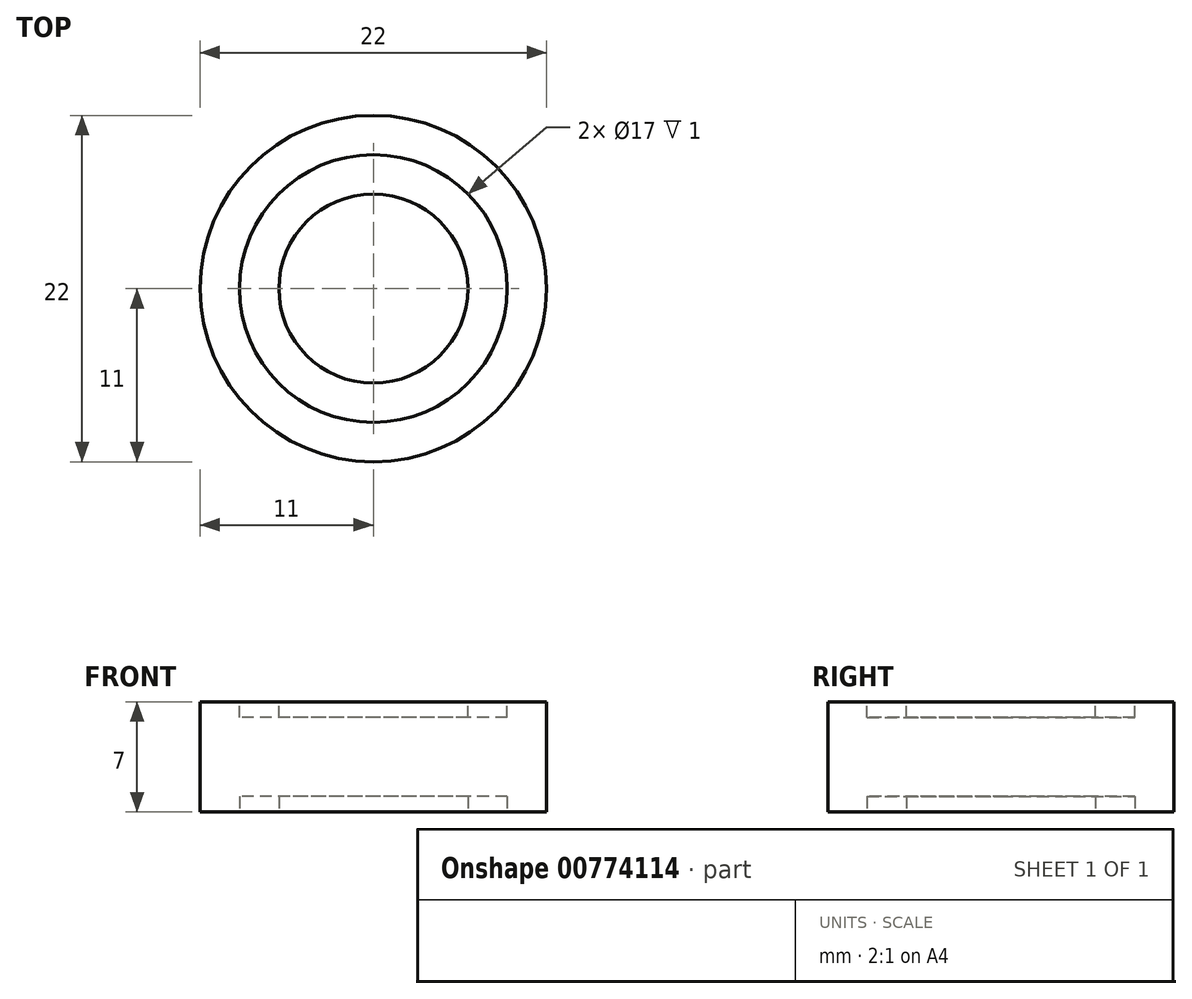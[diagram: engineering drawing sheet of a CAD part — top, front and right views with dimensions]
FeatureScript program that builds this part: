
annotation { "Feature Type Name" : "Feature", "Feature Type Description" : "" }
export const myFeature = defineFeature(function(context is Context, id is Id, definition is map)
    precondition{}
    {
        {
            var Q0;
            Q0=qCreatedBy(makeId("Top.planeOp"),FACE);
            var sketch = newSketch(context, id + "F0", { "sketchPlane" : qUnion([Q0])});
            skCircle(sketch, "E0", {"center": v(0, 0) * mm, "radius": 11 * mm});
            skSolve(sketch);
        }
        {
            var Q0;
            Q0=makeQuery(id+"F0.imprint","IMPRINT",FACE,{"disambiguationData":[TD([[makeQuery(id+"F0.imprint","IMPRINT",EDGE,{"derivedFrom":sQuery(id+"F0.wireOp",EDGE,"E0")}),1.0]])]});
            extrude(context, id + "F1", {"entities" : qUnion([Q0]), "depth" : 3.5 * mm, "offsetDistance" : 25 * mm, "hasSecondDirection" : true, "secondDirectionOppositeDirection" : true, "secondDirectionDepth" : 3.5 * mm});
        }
        {
            var Q0;
            Q0=qCreatedBy(makeId("Top.planeOp"),FACE);
            var sketch = newSketch(context, id + "F2", { "sketchPlane" : qUnion([Q0])});
            skCircle(sketch, "E1.cCircle", {"center": v(0, 22.13) * mm, "radius": 7.5 * mm, "construction": true});
            skLineSegment(sketch, "E1.0", {"start": v(4.33, 14.63) * mm, "end": v(-4.33, 14.63) * mm});
            skLineSegment(sketch, "E1.1", {"start": v(-4.33, 14.63) * mm, "end": v(-8.66, 22.13) * mm});
            skLineSegment(sketch, "E1.2", {"start": v(-8.66, 22.13) * mm, "end": v(-4.33, 29.63) * mm});
            skLineSegment(sketch, "E1.3", {"start": v(-4.33, 29.63) * mm, "end": v(4.33, 29.63) * mm});
            skLineSegment(sketch, "E1.4", {"start": v(4.33, 29.63) * mm, "end": v(8.66, 22.13) * mm});
            skLineSegment(sketch, "E1.5", {"start": v(8.66, 22.13) * mm, "end": v(4.33, 14.63) * mm});
            skPoint(sketch, "E1.0.midPoint", {"position": v(0, 14.63) * mm});
            skCircle(sketch, "E2.cCircle", {"center": v(0, 22.13) * mm, "radius": 5 * mm, "construction": true});
            skLineSegment(sketch, "E2.0", {"start": v(2.89, 17.13) * mm, "end": v(-2.89, 17.13) * mm});
            skLineSegment(sketch, "E2.1", {"start": v(-2.89, 17.13) * mm, "end": v(-5.77, 22.13) * mm});
            skLineSegment(sketch, "E2.2", {"start": v(-5.77, 22.13) * mm, "end": v(-2.89, 27.13) * mm});
            skLineSegment(sketch, "E2.3", {"start": v(-2.89, 27.13) * mm, "end": v(2.89, 27.13) * mm});
            skLineSegment(sketch, "E2.4", {"start": v(2.89, 27.13) * mm, "end": v(5.77, 22.13) * mm});
            skLineSegment(sketch, "E2.5", {"start": v(5.77, 22.13) * mm, "end": v(2.89, 17.13) * mm});
            skPoint(sketch, "E2.0.midPoint", {"position": v(0, 17.13) * mm});
            skCircle(sketch, "E3", {"center": v(0, 22.13) * mm, "radius": 5 * mm});
            skSolve(sketch);
        }
        {
            var Q0;
            Q0=makeQuery(id+"F2.imprint","IMPRINT",FACE,{"disambiguationData":[TD([[makeQuery(id+"F2.imprint","IMPRINT",EDGE,{"derivedFrom":sQuery(id+"F2.wireOp",EDGE,"E1.0")}),-1.0]])]});
            var Q1;
            {var subQ0=sQuery(id+"F2.wireOp",EDGE,"E2.1");var subQ1=sQuery(id+"F2.wireOp",EDGE,"E2.0");var subQ2=makeQuery(id+"F2.imprint","INTERSECT",VERTEX,{"derivedFrom":[subQ1,subQ0]});Q1=makeQuery(id+"F2.imprint","IMPRINT",FACE,{"disambiguationData":[TD([[makeQuery(id+"F2.imprint","IMPRINT",EDGE,{"disambiguationData":[TD([[subQ2,1.0]])],"derivedFrom":subQ1}),-1.0]])]});}
            var Q2;
            {var subQ0=sQuery(id+"F2.wireOp",EDGE,"E2.2");var subQ1=sQuery(id+"F2.wireOp",EDGE,"E2.1");var subQ2=makeQuery(id+"F2.imprint","INTERSECT",VERTEX,{"derivedFrom":[subQ1,subQ0]});Q2=makeQuery(id+"F2.imprint","IMPRINT",FACE,{"disambiguationData":[TD([[makeQuery(id+"F2.imprint","IMPRINT",EDGE,{"disambiguationData":[TD([[subQ2,1.0]])],"derivedFrom":subQ1}),-1.0]])]});}
            var Q3;
            {var subQ0=sQuery(id+"F2.wireOp",EDGE,"E2.3");var subQ1=sQuery(id+"F2.wireOp",EDGE,"E2.2");var subQ2=makeQuery(id+"F2.imprint","INTERSECT",VERTEX,{"derivedFrom":[subQ1,subQ0]});Q3=makeQuery(id+"F2.imprint","IMPRINT",FACE,{"disambiguationData":[TD([[makeQuery(id+"F2.imprint","IMPRINT",EDGE,{"disambiguationData":[TD([[subQ2,1.0]])],"derivedFrom":subQ1}),-1.0]])]});}
            var Q4;
            {var subQ0=sQuery(id+"F2.wireOp",EDGE,"E2.4");var subQ1=sQuery(id+"F2.wireOp",EDGE,"E2.3");var subQ2=makeQuery(id+"F2.imprint","INTERSECT",VERTEX,{"derivedFrom":[subQ1,subQ0]});Q4=makeQuery(id+"F2.imprint","IMPRINT",FACE,{"disambiguationData":[TD([[makeQuery(id+"F2.imprint","IMPRINT",EDGE,{"disambiguationData":[TD([[subQ2,1.0]])],"derivedFrom":subQ1}),-1.0]])]});}
            var Q5;
            {var subQ0=sQuery(id+"F2.wireOp",EDGE,"E2.5");var subQ1=sQuery(id+"F2.wireOp",EDGE,"E2.4");var subQ2=makeQuery(id+"F2.imprint","INTERSECT",VERTEX,{"derivedFrom":[subQ1,subQ0]});Q5=makeQuery(id+"F2.imprint","IMPRINT",FACE,{"disambiguationData":[TD([[makeQuery(id+"F2.imprint","IMPRINT",EDGE,{"disambiguationData":[TD([[subQ2,1.0]])],"derivedFrom":subQ1}),-1.0]])]});}
            var Q6;
            {var subQ0=sQuery(id+"F2.wireOp",EDGE,"E2.5");var subQ1=sQuery(id+"F2.wireOp",EDGE,"E2.0");var subQ2=makeQuery(id+"F2.imprint","INTERSECT",VERTEX,{"derivedFrom":[subQ1,subQ0]});Q6=makeQuery(id+"F2.imprint","IMPRINT",FACE,{"disambiguationData":[TD([[makeQuery(id+"F2.imprint","IMPRINT",EDGE,{"disambiguationData":[TD([[subQ2,-1.0]])],"derivedFrom":subQ1}),-1.0]])]});}
            extrude(context, id + "F3", {"entities" : qUnion([Q0, Q1, Q2, Q3, Q4, Q5, Q6]), "depth" : 3.5 * mm, "offsetDistance" : 25 * mm, "hasSecondDirection" : true, "secondDirectionOppositeDirection" : true, "secondDirectionDepth" : 3.5 * mm});
        }
        {
            var Q0;
            Q0=makeQuery(id+"F1.opExtrude","CAP_FACE",FACE,{"disambiguationData":[OSD([sQuery(id+"F0.wireOp",EDGE,"E0")])],"isStart":false});
            var sketch = newSketch(context, id + "F4", { "sketchPlane" : qUnion([Q0])});
            skPoint(sketch, "E4", {"position": v(0, 11) * mm});
            skCircle(sketch, "E5", {"center": v(0, 0) * mm, "radius": 11 * mm});
            skCircle(sketch, "E6", {"center": v(0, 0) * mm, "radius": 8.5 * mm});
            skCircle(sketch, "E7", {"center": v(0, 0) * mm, "radius": 6 * mm});
            skSolve(sketch);
        }
        {
            var Q0;
            Q0=makeQuery(id+"F4.imprint","IMPRINT",FACE,{"disambiguationData":[TD([[makeQuery(id+"F4.imprint","IMPRINT",EDGE,{"derivedFrom":sQuery(id+"F4.wireOp",EDGE,"E6")}),1.0]])]});
            extrude(context, id + "F5", {"entities" : qUnion([Q0]), "operationType" : NewBodyOperationType.REMOVE, "oppositeDirection" : true, "depth" : 1 * mm, "offsetDistance" : 25 * mm});
        }
        {
            var Q0;
            Q0=makeQuery(id+"F1.opExtrude","SWEPT_BODY",BODY,{"disambiguationData":[OSD([sQuery(id+"F0.wireOp",EDGE,"E0")])]});
            var Q1;
            Q1=qCreatedBy(makeId("Top.planeOp"),FACE);
            mirror(context, id + "F6", {"operationType" : NewBodyOperationType.INTERSECT, "entities" : qUnion([Q0]), "mirrorPlane" : qUnion([Q1])});
        }
    });
